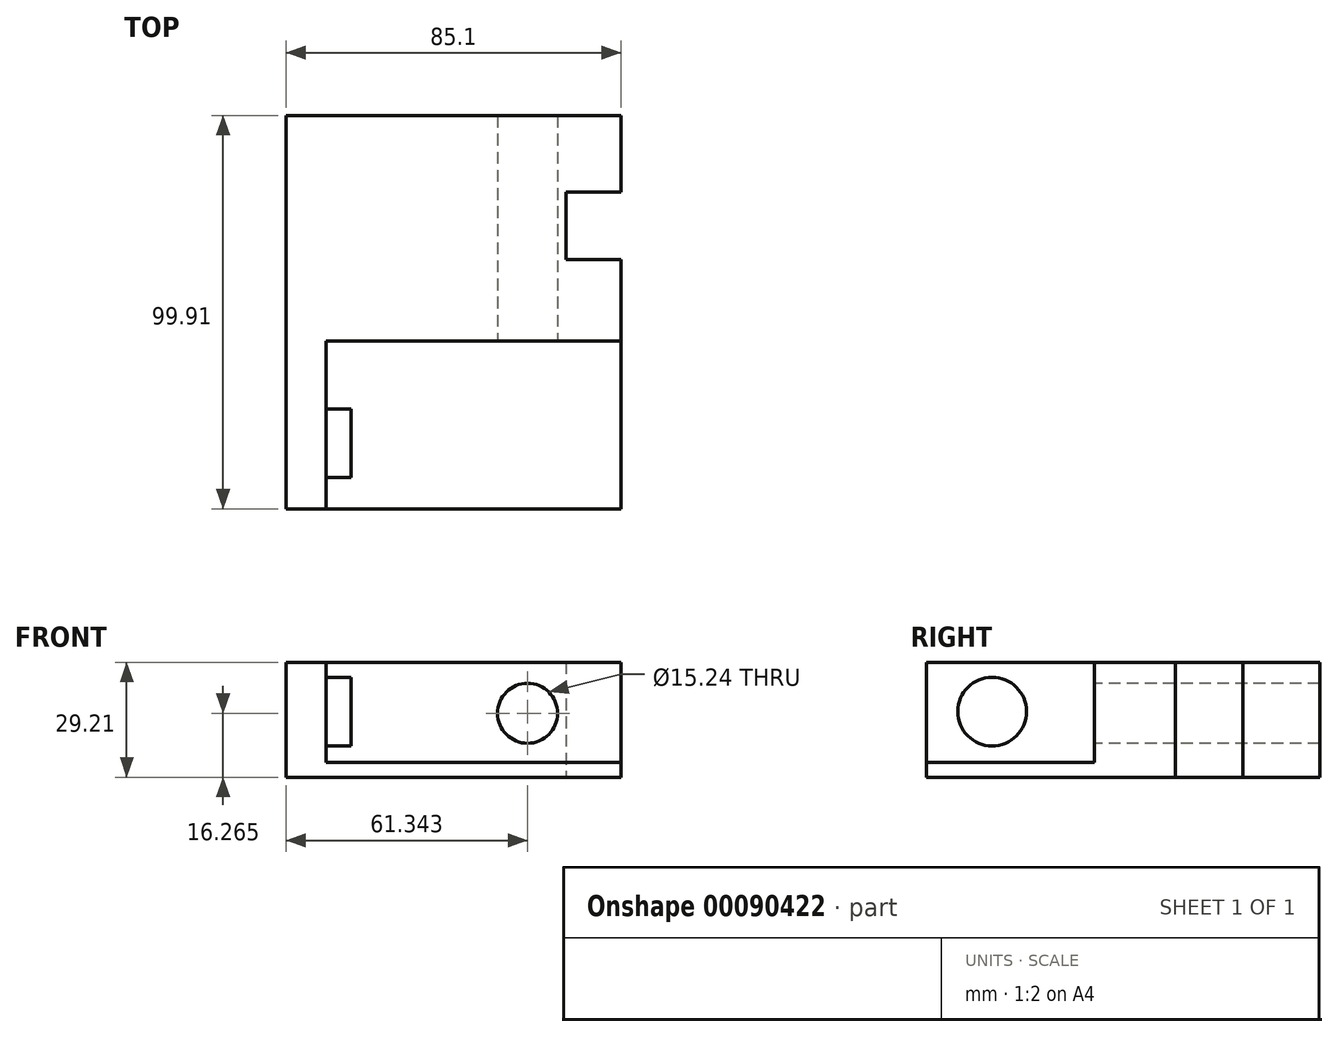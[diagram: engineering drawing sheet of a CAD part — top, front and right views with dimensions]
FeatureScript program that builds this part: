
annotation { "Feature Type Name" : "Feature", "Feature Type Description" : "" }
export const myFeature = defineFeature(function(context is Context, id is Id, definition is map)
    precondition{}
    {
        {
            var Q0;
            Q0=qCreatedBy(makeId("Top.planeOp"),FACE);
            var sketch = newSketch(context, id + "F0", { "sketchPlane" : qUnion([Q0])});
            skLineSegment(sketch, "E0", {"start": v(-39.5, 35.58) * mm, "end": v(-39.5, -57.94) * mm});
            skLineSegment(sketch, "E1", {"start": v(-39.5, -57.94) * mm, "end": v(45.6, -57.94) * mm});
            skLineSegment(sketch, "E2", {"start": v(45.6, -57.94) * mm, "end": v(45.6, 5.37) * mm});
            skLineSegment(sketch, "E3", {"start": v(45.6, 5.37) * mm, "end": v(31.66, 5.37) * mm});
            skLineSegment(sketch, "E4", {"start": v(31.66, 5.37) * mm, "end": v(31.66, 22.5) * mm});
            skLineSegment(sketch, "E5", {"start": v(31.66, 22.5) * mm, "end": v(45.6, 22.5) * mm});
            skLineSegment(sketch, "E6", {"start": v(45.6, 22.5) * mm, "end": v(45.6, 41.97) * mm});
            skLineSegment(sketch, "E7", {"start": v(45.6, 41.97) * mm, "end": v(-39.5, 41.97) * mm});
            skLineSegment(sketch, "E8", {"start": v(-39.5, 41.97) * mm, "end": v(-39.5, 35.58) * mm});
            skSolve(sketch);
        }
        {
            var Q0;
            Q0 = qSketchRegion(id + "F0", true);
            extrude(context, id + "F1", {"entities" : qUnion([Q0]), "depth" : 3.8 * mm});
        }
        {
            var Q0;
            Q0=makeQuery(id+"F1.opExtrude","CAP_FACE",FACE,{"disambiguationData":[OSD([sQuery(id+"F0.wireOp",EDGE,"E0"),sQuery(id+"F0.wireOp",EDGE,"E1"),sQuery(id+"F0.wireOp",EDGE,"E2"),sQuery(id+"F0.wireOp",EDGE,"E3"),sQuery(id+"F0.wireOp",EDGE,"E4"),sQuery(id+"F0.wireOp",EDGE,"E5"),sQuery(id+"F0.wireOp",EDGE,"E6"),sQuery(id+"F0.wireOp",EDGE,"E7"),sQuery(id+"F0.wireOp",EDGE,"E8")])],"isStart":false});
            var sketch = newSketch(context, id + "F2", { "sketchPlane" : qUnion([Q0])});
            skLineSegment(sketch, "E9", {"start": v(-39.5, 41.97) * mm, "end": v(-39.5, -57.94) * mm});
            skLineSegment(sketch, "E10", {"start": v(-39.5, -57.94) * mm, "end": v(-29.33, -57.94) * mm});
            skLineSegment(sketch, "E11", {"start": v(-29.33, -57.94) * mm, "end": v(-29.33, -15.25) * mm});
            skLineSegment(sketch, "E12", {"start": v(-29.33, -15.25) * mm, "end": v(45.6, -15.25) * mm});
            skLineSegment(sketch, "E13", {"start": v(45.6, -15.25) * mm, "end": v(45.6, 5.37) * mm});
            skLineSegment(sketch, "E14", {"start": v(45.6, 5.37) * mm, "end": v(31.66, 5.37) * mm});
            skLineSegment(sketch, "E15", {"start": v(31.66, 5.37) * mm, "end": v(31.66, 22.5) * mm});
            skLineSegment(sketch, "E16", {"start": v(31.66, 22.5) * mm, "end": v(45.6, 22.5) * mm});
            skLineSegment(sketch, "E17", {"start": v(45.6, 22.5) * mm, "end": v(45.6, 41.97) * mm});
            skLineSegment(sketch, "E18", {"start": v(45.6, 41.97) * mm, "end": v(-39.5, 41.97) * mm});
            skSolve(sketch);
        }
        {
            var Q0;
            Q0 = qSketchRegion(id + "F2", true);
            extrude(context, id + "F3", {"entities" : qUnion([Q0]), "operationType" : NewBodyOperationType.ADD, "depth" : 25.4 * mm});
        }
        {
            var Q0;
            Q0=makeQuery(id+"F3.opExtrude","SWEPT_FACE",FACE,{"disambiguationData":[OSD([sQuery(id+"F2.wireOp",EDGE,"E11")])]});
            var sketch = newSketch(context, id + "F4", { "sketchPlane" : qUnion([Q0])});
            skCircle(sketch, "E19", {"center": v(-41.25, 16.7) * mm, "radius": 8.72 * mm});
            skPoint(sketch, "E19.first.point", {"position": v(-41.53, 7.99) * mm});
            skPoint(sketch, "E19.second.point", {"position": v(-40.66, 25.41) * mm});
            skPoint(sketch, "E19.third.point", {"position": v(-33.69, 21.06) * mm});
            skSolve(sketch);
        }
        {
            var Q0;
            Q0 = qSketchRegion(id + "F4", true);
            extrude(context, id + "F5", {"entities" : qUnion([Q0]), "operationType" : NewBodyOperationType.ADD, "depth" : 6.35 * mm});
        }
        {
            var Q0;
            Q0=makeQuery(id+"F3.opExtrude","SWEPT_FACE",FACE,{"disambiguationData":[OSD([sQuery(id+"F2.wireOp",EDGE,"E12")])]});
            var sketch = newSketch(context, id + "F6", { "sketchPlane" : qUnion([Q0])});
            skCircle(sketch, "E20", {"center": v(21.84, 16.26) * mm, "radius": 8.28 * mm});
            skPoint(sketch, "E20.first.point", {"position": v(22.07, 24.54) * mm});
            skPoint(sketch, "E20.second.point", {"position": v(21.78, 7.99) * mm});
            skPoint(sketch, "E20.third.point", {"position": v(27.88, 10.6) * mm});
            skSolve(sketch);
        }
        {
            var Q0;
            Q0=sQuery(id+"F6.wireOp",VERTEX,"E20.center");
            var Q1;
            Q1=makeQuery(id+"F1.opExtrude","SWEPT_BODY",BODY,{"disambiguationData":[OSD([sQuery(id+"F0.wireOp",EDGE,"E0"),sQuery(id+"F0.wireOp",EDGE,"E1"),sQuery(id+"F0.wireOp",EDGE,"E2"),sQuery(id+"F0.wireOp",EDGE,"E3"),sQuery(id+"F0.wireOp",EDGE,"E4"),sQuery(id+"F0.wireOp",EDGE,"E5"),sQuery(id+"F0.wireOp",EDGE,"E6"),sQuery(id+"F0.wireOp",EDGE,"E7"),sQuery(id+"F0.wireOp",EDGE,"E8")])]});
            hole(context, id + "F7", {"style" : HoleStyle.SIMPLE, "endStyle" : HoleEndStyle.THROUGH, "holeDiameter" : 15.24 * mm, "locations" : qUnion([Q0]), "scope" : qUnion([Q1]), "isTappedThrough" : true});
        }
    });
